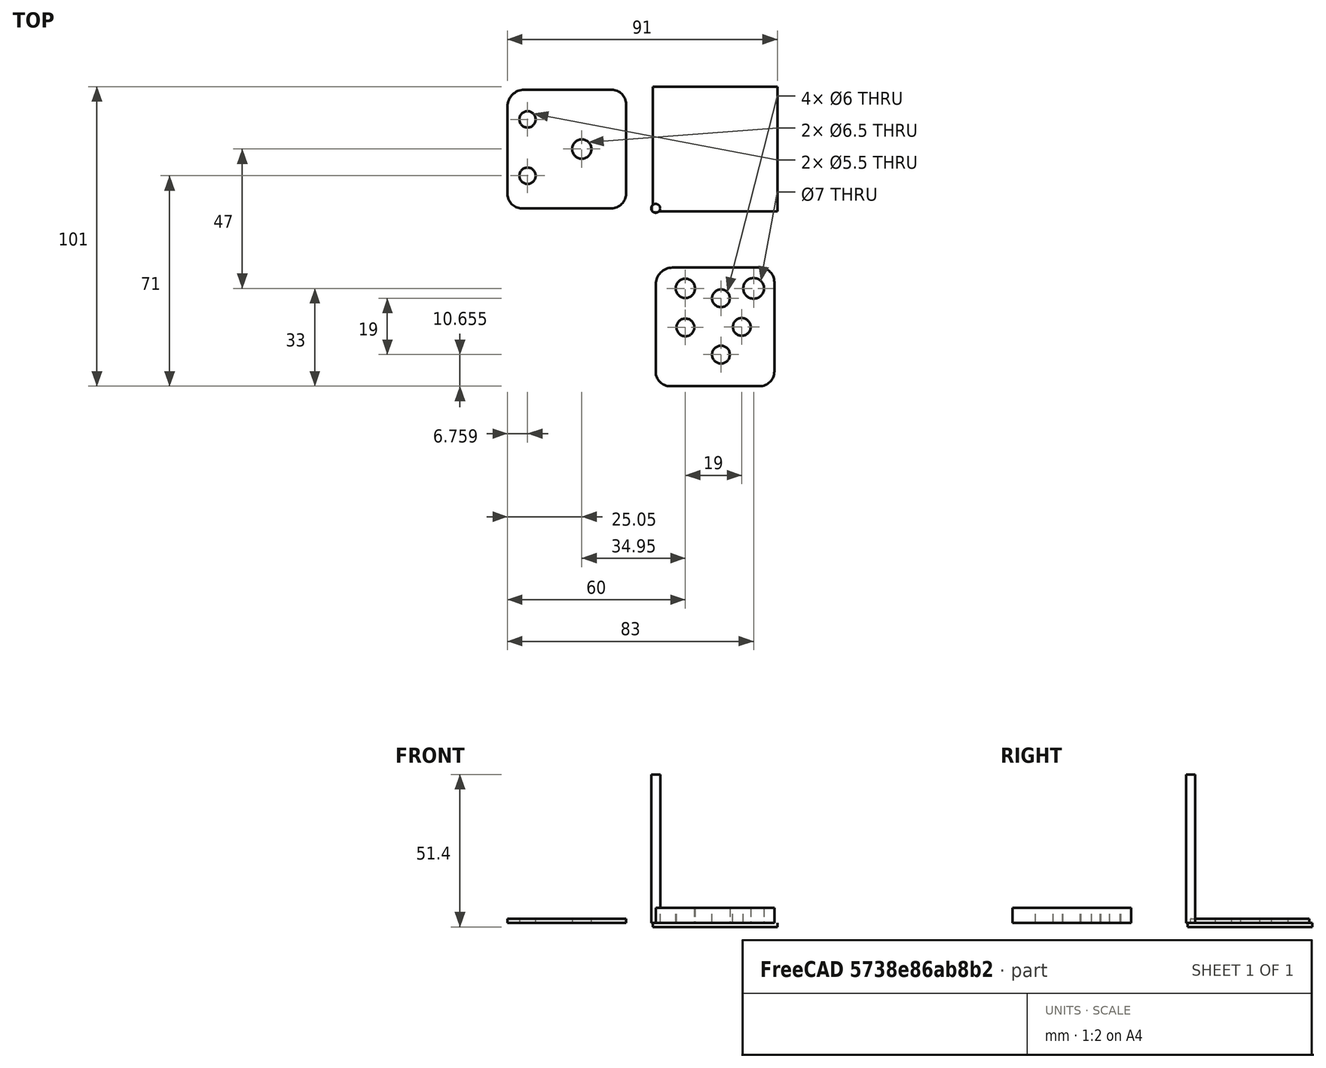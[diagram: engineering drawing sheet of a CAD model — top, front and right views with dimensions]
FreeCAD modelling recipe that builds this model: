
FCSTD DOCUMENT  (FreeCAD 0.19R24276 (Git))
Label: AdaptateurAlim
License: All rights reserved
LicenseURL: http://en.wikipedia.org/wiki/All_rights_reserved
objects: Sketcher::SketchObject×8, PartDesign::Pocket×5, Path::FeaturePython×5, PartDesign::Pad×3, PartDesign::Body×3, Part::FeaturePython×3, App::DocumentObjectGroup×2, App::FeaturePython×1, Path::FeatureCompoundPython×1, Mesh::FeaturePython×1
note: 32 computed .brp shape members not serialized (recipe doc carries the construction recipe); baked Part::Feature solids carry a one-line shape summary decoded from their .brp

FEATURE [Sketcher::SketchObject] Sketch
  FullyConstrained = false
  MapMode = 5
  Support = -> [XY_Plane]
  sketch-geometry (4):
    g0: LineSegment StartX=0 StartY=40 StartZ=0 EndX=40 EndY=40 EndZ=0
    g1: LineSegment StartX=40 StartY=40 StartZ=0 EndX=40 EndY=0 EndZ=0
    g2: LineSegment StartX=40 StartY=0 StartZ=0 EndX=0 EndY=0 EndZ=0
    g3: LineSegment StartX=0 StartY=0 StartZ=0 EndX=0 EndY=40 EndZ=0
  constraints (10):
    c: Coincident(g0,g1)
    c: Coincident(g1,g2)
    c: Coincident(g2,g3)
    c: Coincident(g3,g0)
    c: Horizontal(g0)
    c: Horizontal(g2)
    c: Vertical(g1)
    c: Vertical(g3)
    c: PointOnObject(g0,g-2)
    c: PointOnObject(g1,g-1)
FEATURE [PartDesign::Pad] Pad
  Direction = (1,1,1)
  Length = 1.4
  Length2 = 100
  Profile = -> Sketch
  Type = 0
FEATURE [Sketcher::SketchObject] Sketch001
  FullyConstrained = false
  MapMode = 5
  Placement = pos=(0,0,1.4) rot=(0,0,1;0rad)
  Support = -> [Pad]
  sketch-geometry (5):
    g0: Circle CenterX=25 CenterY=20 CenterZ=0 NormalX=0 NormalY=0 NormalZ=1 AngleXU=0 Radius=3.1
    g1: Circle CenterX=7 CenterY=10 CenterZ=0 NormalX=0 NormalY=0 NormalZ=1 AngleXU=0 Radius=3
    g2: Circle CenterX=7 CenterY=29 CenterZ=0 NormalX=0 NormalY=0 NormalZ=1 AngleXU=0 Radius=3
    g3: Circle CenterX=33 CenterY=10 CenterZ=0 NormalX=0 NormalY=0 NormalZ=1 AngleXU=0 Radius=3.25
    g4: Circle CenterX=25 CenterY=10 CenterZ=0 NormalX=0 NormalY=0 NormalZ=1 AngleXU=0 Radius=3.35
  constraints (12):
    c: Diameter(g0) = 6.2
    c: DistanceX(g-1,g0) = 25
    c: Diameter(g2) = 6
    c: Diameter(g1) = 6
    c: DistanceX(g-1,g1) = 7
    c: DistanceX(g-1,g2) = 7
    c: DistanceY(g1,g2) = 19
    c: DistanceY(g-1,g1) = 10
    c: Diameter(g3) = 6.5
    c: Diameter(g4) = 6.7
    c: DistanceX(g-1,g3) = 33
    c: DistanceX(g-1,g4) = 25
FEATURE [PartDesign::Pocket] Pocket
  BaseFeature = -> Pad
  Length = 5
  Length2 = 100
  Profile = -> Sketch001
  Type = 1
FEATURE [PartDesign::Body] Body
  Group = -> [Sketch,Pad,Sketch001,Pocket]
  Origin = -> Origin
  Tip = -> Pocket
FEATURE [App::FeaturePython] SetupSheet  # Path/CAM operation (typed FeaturePython)
  ClearanceHeightExpression = OpStockZMax+SetupSheet.ClearanceHeightOffset
  ClearanceHeightOffset = 5
  CoolantMode = 0
  CoolantModes = None | Flood | Mist
  FinalDepthExpression = OpFinalDepth
  HorizRapid = 0
  SafeHeightExpression = OpStockZMax+SetupSheet.SafeHeightOffset
  SafeHeightOffset = 3
  StartDepthExpression = OpStartDepth
  StepDownExpression = OpToolDiameter
  VertRapid = 0
FEATURE [Part::FeaturePython] Clone  label="Model-Body"  # Draft clone (typed FeaturePython)
  AttacherType = Attacher::AttachEngine3D
  Fuse = false
  Objects = -> [Body]
  PathResource = Model
  Placement = pos=(0,0,-1.4) rot=(0,0,1;0rad)
  Scale = (1,1,1)
FEATURE [App::DocumentObjectGroup] Model
  Group = -> [Clone]
FEATURE [Part::FeaturePython] ToolBit  label="Endmill"  # Path/CAM toolbit (typed FeaturePython)
  BitPropertyNames = Chipload | CuttingEdgeHeight | Diameter | Flutes | Length | Material | ShankDiameter
  BitShape = /Volumes/SSD/Applications/FreeCAD_0.19-24276.app/Contents/Resources/Mod/Path/Tools/Shape/endmill.fcstd
  Chipload = 0
  CuttingEdgeHeight = 30
  Diameter = 3
  Flutes = 0
  Length = 50
  Material = 0
  ShankDiameter = 3
  ShapeName = endmill
FEATURE [Path::FeaturePython] TC__Default_Tool  label="TC: Default Tool"  # Path/CAM operation (typed FeaturePython)
  HorizFeed = 0
  HorizRapid = 0
  SpindleDir = 0
  SpindleSpeed = 0
  Tool = -> ToolBit
  ToolNumber = 1
  VertFeed = 0
  VertRapid = 0
  expr: VertRapid = SetupSheet.VertRapid
  expr: HorizRapid = SetupSheet.HorizRapid
FEATURE [App::DocumentObjectGroup] Tools
  Group = -> [TC__Default_Tool]
FEATURE [Part::FeaturePython] Stock  # WARN: FeaturePython — macro-defined, semantics opaque (R4)
  Base = -> Model
  ExtXneg = 1
  ExtXpos = 1
  ExtYneg = 1
  ExtYpos = 1
  ExtZneg = 0
  ExtZpos = 0
  Placement = pos=(0,0,-1.4) rot=(0,0,1;0rad)
  StockType = FromBase
FEATURE [Path::FeaturePython] Pocket_Shape  # Path/CAM operation (typed FeaturePython)
  Active = true
  AreaParams:
    Tolerance = 1e-07
    FitArcs = True
    Simplify = False
    CleanDistance = 0.0
    Accuracy = 0.01
    Unit = 1.0
    MinArcPoints = 4
    MaxArcPoints = 100
    ClipperScale = 10000000.0
    Fill = 0
    Coplanar = 0
    Reorient = True
    Outline = False
    Explode = False
    OpenMode = 0
    Deflection = 0.01
    SubjectFill = 0
    ClipFill = 0
    Offset = 0.0
    ExtraPass = 0
    Stepover = 0.0
    LastStepover = 0.0
    JoinType = 0
    EndType = 0
    MiterLimit = 2.0
    RoundPrecision = 0.0
    PocketMode = 4
    ToolRadius = 1.5
    PocketExtraOffset = 0.0
    PocketStepover = 3.0
    PocketLastStepover = 0.0
    FromCenter = True
    Angle = 45.0
    AngleShift = 0.0
    Shift = 0.0
    Thicken = False
    SectionCount = -1
    Stepdown = 1.0
    SectionOffset = 0.0
    SectionTolerance = 1e-06
    SectionMode = 2
    Project = False
  AttemptInverseAngle = true
  Base = -> [Clone]
  ClearanceHeight = 5
  CoolantMode = None
  CutMode = 0
  CycleTime = Erreur de temps de cycle
  EnableRotation = 0
  ExtensionCorners = true
  ExtensionLengthDefault = 1.5
  ExtraOffset = 0
  FinalDepth = -1.4
  FinishDepth = 0
  InverseAngle = false
  KeepToolDown = false
  LimitDepthToFace = true
  MinTravel = false
  OffsetPattern = 3
  OpFinalDepth = -1.4
  OpStartDepth = 0
  OpStockZMax = 0
  OpStockZMin = -1.4
  OpToolDiameter = 3
  PathParams = {'orientation': 1, 'feedrate': 0.0, 'feedrate_v': 0.0, 'verbose': True, 'resume_height': 3.0, 'retraction': 5.0, 'return_end': True, 'preamble': False, 'start': Vector (24.538343771145534, 21.52480244665558, 5.0)}
  ReverseDirection = false
  SafeHeight = 3
  StartAt = 0
  StartDepth = 0
  StartPoint = (0,0,0)
  StepDown = 1.4
  StepOver = 100
  ToolController = -> TC__Default_Tool
  UseOutline = false
  UseStartPoint = false
  ZigZagAngle = 45
  expr: StartDepth = OpStartDepth
  expr: FinalDepth = OpFinalDepth
  expr: StepDown = 1.4
  expr: SafeHeight = OpStockZMax + SetupSheet.SafeHeightOffset
  expr: ClearanceHeight = OpStockZMax + SetupSheet.ClearanceHeightOffset
  expr: ExtensionLengthDefault = OpToolDiameter / 2
FEATURE [Path::FeaturePython] Profile  # Path/CAM operation (typed FeaturePython)
  Active = true
  AreaParams:
    Tolerance = 1e-07
    FitArcs = True
    Simplify = False
    CleanDistance = 0.0
    Accuracy = 0.01
    Unit = 1.0
    MinArcPoints = 4
    MaxArcPoints = 100
    ClipperScale = 10000000.0
    Fill = 0
    Coplanar = 0
    Reorient = True
    Outline = False
    Explode = False
    OpenMode = 0
    Deflection = 0.01
    SubjectFill = 0
    ClipFill = 0
    Offset = 1.5
    ExtraPass = 0
    Stepover = 0.0
    LastStepover = 0.0
    JoinType = 0
    EndType = 0
    MiterLimit = 2.0
    RoundPrecision = 0.0
    PocketMode = 0
    ToolRadius = 1.0
    PocketExtraOffset = 0.0
    PocketStepover = 0.0
    PocketLastStepover = 0.0
    FromCenter = False
    Angle = 45.0
    AngleShift = 0.0
    Shift = 0.0
    Thicken = False
    SectionCount = -1
    Stepdown = 1.0
    SectionOffset = 0.0
    SectionTolerance = 1e-06
    SectionMode = 2
    Project = False
  AttemptInverseAngle = true
  Base = -> [Clone]
  ClearanceHeight = 5
  CoolantMode = None
  CycleTime = Erreur de temps de cycle
  Direction = 0
  EnableRotation = 0
  FinalDepth = -1.4
  HandleMultipleFeatures = 0
  InverseAngle = false
  JoinType = 0
  LimitDepthToFace = true
  MiterLimit = 0.1
  OffsetExtra = 0
  OpFinalDepth = -1.4
  OpStartDepth = 0
  OpStockZMax = 0
  OpStockZMin = -1.4
  OpToolDiameter = 3
  PathParams = {'orientation': 1, 'feedrate': 0.0, 'feedrate_v': 0.0, 'verbose': True, 'resume_height': 3.0, 'retraction': 5.0, 'return_end': True, 'preamble': False}
  ReverseDirection = false
  SafeHeight = 3
  Side = 0
  StartDepth = 0
  StartPoint = (0,0,0)
  StepDown = 1.4
  ToolController = -> TC__Default_Tool
  UseComp = true
  UseStartPoint = false
  processCircles = false
  processHoles = false
  processPerimeter = true
  expr: StartDepth = OpStartDepth
  expr: FinalDepth = OpFinalDepth
  expr: StepDown = 1.4
  expr: SafeHeight = OpStockZMax + SetupSheet.SafeHeightOffset
  expr: ClearanceHeight = OpStockZMax + SetupSheet.ClearanceHeightOffset
FEATURE [Path::FeaturePython] DressupTag  # Path/CAM operation (typed FeaturePython)
  Angle = 45
  Base = -> Profile
  Height = 0.7
  Positions = (4) [(41.5,20,0),(20,-1.5,0),(-1.5,20,0),(20,41.5,0)]
  Radius = 0
  SegmentationFactor = 50
  Width = 4
FEATURE [Path::FeatureCompoundPython] Operations  # Path/CAM operation (typed FeaturePython)
  Group = -> [Pocket_Shape,DressupTag]
  UsePlacements = false
FEATURE [Path::FeaturePython] Job  # Path/CAM operation (typed FeaturePython)
  CycleTime = 00:00:00
  Fixtures = G54
  GeometryTolerance = 0.01
  LastPostProcessDate = 2021-04-25 22:09:16.791276
  LastPostProcessOutput = /Volumes/SSD/Dev/CNC/MiscCNC/AdaptateurAlim.gcode
  Model = -> Model
  Operations = -> Operations
  OrderOutputBy = 0
  PostProcessor = 1
  PostProcessorOutputFile = /Volumes/SSD/Dev/CNC/MiscCNC/AdaptateurAlim.gcode
  SetupSheet = -> SetupSheet
  SplitOutput = false
  Stock = -> Stock
  Tools = -> Tools
FEATURE [Mesh::FeaturePython] CutMaterial001  # WARN: FeaturePython — macro-defined, semantics opaque (R4)
FEATURE [Sketcher::SketchObject] Sketch002
  FullyConstrained = false
  MapMode = 5
  Support = -> [XY_Plane001]
  sketch-geometry (11):
    g0: LineSegment StartX=-14.97 StartY=0 StartZ=0 EndX=-45.1431 EndY=0 EndZ=0
    g1: LineSegment StartX=-50 StartY=4.85685 StartZ=0 EndX=-50 EndY=34.3431 EndZ=0
    g2: LineSegment StartX=-44.3431 StartY=40 StartZ=0 EndX=-14.8569 EndY=40 EndZ=0
    g3: LineSegment StartX=-10 StartY=35.1431 StartZ=0 EndX=-10 EndY=4.96999 EndZ=0
    g4: ArcOfCircle CenterX=-44.3431 CenterY=34.3431 CenterZ=0 NormalX=0 NormalY=0 NormalZ=1 AngleXU=0 Radius=5.65685 StartAngle=1.5708 EndAngle=3.14159
    g5: ArcOfCircle CenterX=-14.8569 CenterY=35.1431 CenterZ=0 NormalX=0 NormalY=0 NormalZ=1 AngleXU=0 Radius=4.85685 StartAngle=0 EndAngle=1.5708
    g6: ArcOfCircle CenterX=-14.97 CenterY=4.96999 CenterZ=0 NormalX=0 NormalY=0 NormalZ=1 AngleXU=0 Radius=4.96999 StartAngle=4.71239 EndAngle=6.28319
    g7: ArcOfCircle CenterX=-45.1431 CenterY=4.85685 CenterZ=0 NormalX=0 NormalY=0 NormalZ=1 AngleXU=0 Radius=4.85685 StartAngle=3.14159 EndAngle=4.71239
    g8: Circle CenterX=-43.2412 CenterY=30 CenterZ=0 NormalX=0 NormalY=0 NormalZ=1 AngleXU=0 Radius=2.75
    g9: Circle CenterX=-43.2412 CenterY=11 CenterZ=0 NormalX=0 NormalY=0 NormalZ=1 AngleXU=0 Radius=2.75
    g10: Circle CenterX=-24.9499 CenterY=20 CenterZ=0 NormalX=0 NormalY=0 NormalZ=1 AngleXU=0 Radius=3.25
  constraints (18):
    c: Horizontal(g0)
    c: Horizontal(g2)
    c: Vertical(g1)
    c: Vertical(g3)
    c: Tangent(g1,g4) = 1.5708
    c: Tangent(g2,g4) = 1.5708
    c: Tangent(g2,g5) = 1.5708
    c: Tangent(g3,g5) = 1.5708
    c: Tangent(g0,g6) = 1.5708
    c: Tangent(g3,g6) = 1.5708
    c: Tangent(g0,g7) = 1.5708
    c: Tangent(g1,g7) = 1.5708
    c: DistanceY(g9,g8) = 19
    c: Diameter(g8) = 5.5
    c: Diameter(g9) = 5.5
    c: DistanceY(g-1,g8) = 30
    c: Diameter(g10) = 6.5
    c: DistanceY(g-1,g10) = 20
FEATURE [PartDesign::Pad] Pad001
  Direction = (1,1,1)
  Length = 1.4
  Length2 = 100
  Profile = -> Sketch002
  Type = 0
FEATURE [PartDesign::Body] Body001
  Group = -> [Sketch002,Pad001]
  Origin = -> Origin001
  Tip = -> Pad001
FEATURE [Sketcher::SketchObject] Sketch003
  FullyConstrained = false
  MapMode = 5
  Support = -> [XY_Plane002]
  sketch-geometry (8):
    g0: LineSegment StartX=5.65685 StartY=-20 StartZ=0 EndX=35.1431 EndY=-20 EndZ=0
    g1: LineSegment StartX=40 StartY=-24.8569 StartZ=0 EndX=40 EndY=-55.03 EndZ=0
    g2: LineSegment StartX=35.03 StartY=-60 StartZ=0 EndX=4.85685 EndY=-60 EndZ=0
    g3: LineSegment StartX=0 StartY=-55.1431 StartZ=0 EndX=0 EndY=-25.6569 EndZ=0
    g4: ArcOfCircle CenterX=5.65685 CenterY=-25.6569 CenterZ=0 NormalX=0 NormalY=0 NormalZ=1 AngleXU=0 Radius=5.65685 StartAngle=1.5708 EndAngle=3.14159
    g5: ArcOfCircle CenterX=35.1431 CenterY=-24.8569 CenterZ=0 NormalX=0 NormalY=0 NormalZ=1 AngleXU=0 Radius=4.85685 StartAngle=0 EndAngle=1.5708
    g6: ArcOfCircle CenterX=35.03 CenterY=-55.03 CenterZ=0 NormalX=0 NormalY=0 NormalZ=1 AngleXU=0 Radius=4.96999 StartAngle=4.71239 EndAngle=6.28319
    g7: ArcOfCircle CenterX=4.85685 CenterY=-55.1431 CenterZ=0 NormalX=0 NormalY=0 NormalZ=1 AngleXU=0 Radius=4.85685 StartAngle=3.14159 EndAngle=4.71239
  constraints (12):
    c: Horizontal(g0)
    c: Horizontal(g2)
    c: Vertical(g1)
    c: Vertical(g3)
    c: Tangent(g0,g4) = 1.5708
    c: Tangent(g3,g4) = 1.5708
    c: Tangent(g0,g5) = 1.5708
    c: Tangent(g1,g5) = 1.5708
    c: Tangent(g1,g6) = 1.5708
    c: Tangent(g2,g6) = 1.5708
    c: Tangent(g2,g7) = 1.5708
    c: Tangent(g3,g7) = 1.5708
FEATURE [PartDesign::Pad] Pad002
  Direction = (1,1,1)
  Length = 5
  Length2 = 100
  Profile = -> Sketch003
  Type = 0
FEATURE [Sketcher::SketchObject] Sketch004  label="Trous fiches mâles"
  FullyConstrained = false
  MapMode = 5
  Placement = pos=(0,0,5) rot=(0,0,1;0rad)
  Support = -> [Pad002]
  sketch-geometry (2):
    g0: Circle CenterX=22 CenterY=-49.3448 CenterZ=0 NormalX=0 NormalY=0 NormalZ=1 AngleXU=0 Radius=3
    g1: Circle CenterX=22 CenterY=-30.3448 CenterZ=0 NormalX=0 NormalY=0 NormalZ=1 AngleXU=0 Radius=3
  constraints (5):
    c: DistanceX(g-1,g1) = 22
    c: DistanceX(g-1,g0) = 22
    c: DistanceY(g0,g1) = 19
    c: Diameter(g1) = 6
    c: Diameter(g0) = 6
FEATURE [PartDesign::Pocket] Pocket001  label="fiches mâles"
  BaseFeature = -> Pad002
  Length = 5
  Length2 = 100
  Profile = -> Sketch004
  Type = 1
FEATURE [Sketcher::SketchObject] Sketch006  label="Trous fiches femelles"
  FullyConstrained = false
  MapMode = 5
  Placement = pos=(0,0,5) rot=(0,0,1;0rad)
  Support = -> [Pocket001]
  sketch-geometry (2):
    g0: Circle CenterX=10 CenterY=-40.1651 CenterZ=0 NormalX=0 NormalY=0 NormalZ=1 AngleXU=0 Radius=3
    g1: Circle CenterX=29 CenterY=-39.9952 CenterZ=0 NormalX=0 NormalY=0 NormalZ=1 AngleXU=0 Radius=3
  constraints (4):
    c: Diameter(g1) = 6
    c: Diameter(g0) = 6
    c: DistanceX(g0,g1) = 19
    c: DistanceX(g-1,g0) = 10
FEATURE [PartDesign::Pocket] Pocket002  label="fiches femelles"
  BaseFeature = -> Pocket001
  Length = 5
  Length2 = 100
  Profile = -> Sketch006
  Type = 1
FEATURE [Sketcher::SketchObject] Sketch007
  FullyConstrained = false
  MapMode = 5
  Placement = pos=(0,0,5) rot=(0,0,1;0rad)
  Support = -> [Pocket002]
  sketch-geometry (2):
    g0: Circle CenterX=33 CenterY=-27 CenterZ=0 NormalX=0 NormalY=0 NormalZ=1 AngleXU=0 Radius=3.5
    g1: LineSegment StartX=-10 StartY=-20 StartZ=0 EndX=50 EndY=-20 EndZ=0
  constraints (4):
    c: Diameter(g0) = 7
    c: Horizontal(g1)
    c: DistanceY(g0) = -27
    c: DistanceX(g0) = 33
FEATURE [PartDesign::Pocket] Pocket003  label="interrupteur"
  BaseFeature = -> Pocket002
  Length = 5
  Length2 = 100
  Profile = -> Sketch007
  Type = 1
FEATURE [Sketcher::SketchObject] Sketch008
  FullyConstrained = true
  MapMode = 5
  Placement = pos=(0,0,5) rot=(0,0,1;0rad)
  Support = -> [Pocket003]
  sketch-geometry (1):
    g0: Circle CenterX=10 CenterY=-27 CenterZ=0 NormalX=0 NormalY=0 NormalZ=1 AngleXU=0 Radius=3.25
  constraints (3):
    c: Diameter(g0) = 6.5
    c: DistanceX(g-1,g0) = 10
    c: DistanceY(g0) = -27
FEATURE [PartDesign::Pocket] Pocket004  label="LED"
  BaseFeature = -> Pocket003
  Length = 5
  Length2 = 100
  Profile = -> Sketch008
  Type = 1
FEATURE [PartDesign::Body] Body002
  Group = -> [Sketch003,Pad002,Sketch004,Pocket001,Sketch006,Pocket002,Sketch007,Pocket003,Sketch008,Pocket004]
  Origin = -> Origin002
  Tip = -> Pocket004
